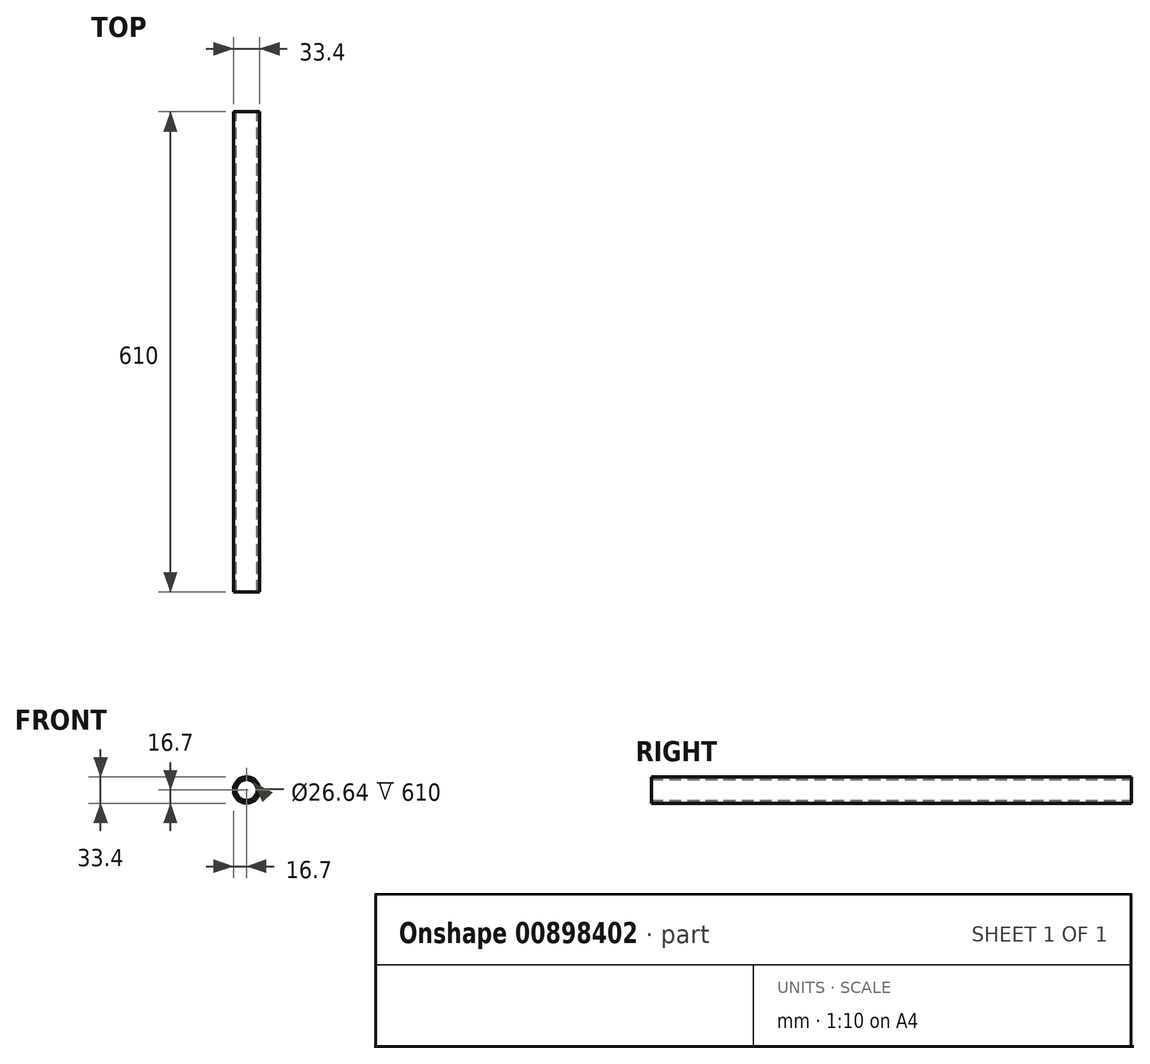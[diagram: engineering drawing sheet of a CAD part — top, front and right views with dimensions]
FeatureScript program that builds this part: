
annotation { "Feature Type Name" : "Feature", "Feature Type Description" : "" }
export const myFeature = defineFeature(function(context is Context, id is Id, definition is map)
    precondition{}
    {
        {
            var Q0;
            Q0=qCreatedBy(makeId("Front.planeOp"),FACE);
            var sketch = newSketch(context, id + "F0", { "sketchPlane" : qUnion([Q0])});
            skCircle(sketch, "E0", {"center": v(0, 0) * mm, "radius": 16.7 * mm});
            skCircle(sketch, "E1", {"center": v(0, 0) * mm, "radius": 13.32 * mm});
            skSolve(sketch);
        }
        {
            var Q0;
            Q0=makeQuery(id+"F0.imprint","IMPRINT",FACE,{"disambiguationData":[TD([[makeQuery(id+"F0.imprint","IMPRINT",EDGE,{"derivedFrom":sQuery(id+"F0.wireOp",EDGE,"E0")}),1.0]])]});
            extrude(context, id + "F1", {"entities" : qUnion([Q0]), "endBound" : BoundingType.SYMMETRIC, "depth" : 610 * mm, "offsetDistance" : 25.4 * mm});
        }
    });
